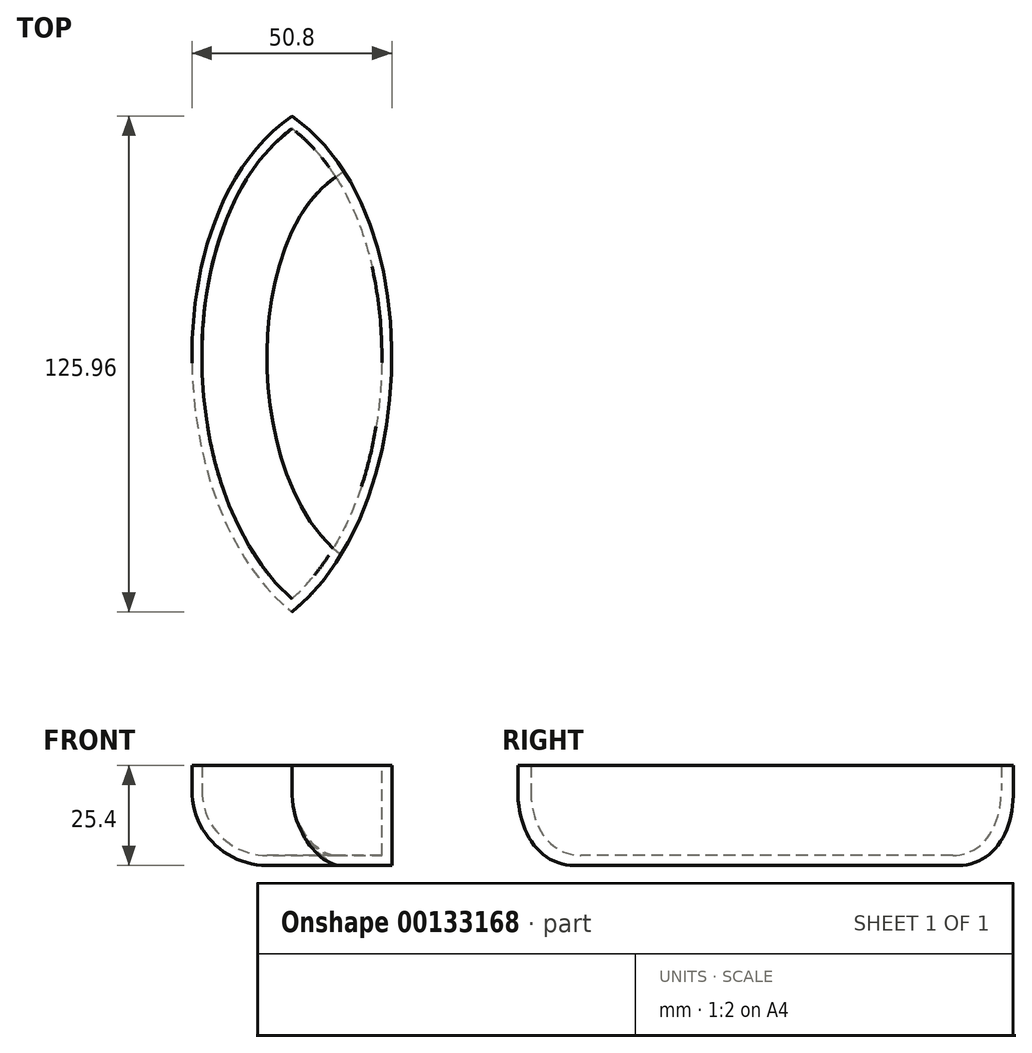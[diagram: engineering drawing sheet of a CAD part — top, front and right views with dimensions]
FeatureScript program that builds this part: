
annotation { "Feature Type Name" : "Feature", "Feature Type Description" : "" }
export const myFeature = defineFeature(function(context is Context, id is Id, definition is map)
    precondition{}
    {
        {
            var Q0;
            Q0=qCreatedBy(makeId("Top.planeOp"),FACE);
            var sketch = newSketch(context, id + "F0", { "sketchPlane" : qUnion([Q0])});
            skFitSpline(sketch, "E0", {"points": [v(0, 61.2) * mm, v(0, -64.75) * mm], "startDerivative": vector(-104.4, -72) * mm, "endDerivative": vector(98.77, -79.04) * mm});
            skFitSpline(sketch, "E1.MirrorCS", {"points": [v(0, 61.2) * mm, v(0, -64.75) * mm], "startDerivative": vector(104.4, -72) * mm, "endDerivative": vector(-98.77, -79.04) * mm});
            skFitSpline(sketch, "E2.MirrorCS", {"points": [v(0, 61.2) * mm, v(0, -64.75) * mm], "startDerivative": vector(104.4, -72) * mm, "endDerivative": vector(-98.77, -79.04) * mm});
            skLineSegment(sketch, "E3", {"start": v(-25.4, 0) * mm, "end": v(25.4, 0) * mm, "construction": true});
            skSolve(sketch);
        }
        {
            var Q0;
            Q0=makeQuery(id+"F0.imprint","IMPRINT",FACE,{"disambiguationData":[TD([[makeQuery(id+"F0.imprint","IMPRINT",EDGE,{"derivedFrom":sQuery(id+"F0.wireOp",EDGE,"E0")}),1.0]])]});
            extrude(context, id + "F1", {"entities" : qUnion([Q0]), "depth" : 25.4 * mm});
        }
        {
            var Q0;
            Q0=makeQuery(id+"F1.opExtrude","CAP_EDGE",EDGE,{"disambiguationData":[OSD([sQuery(id+"F0.wireOp",EDGE,"E2.MirrorCS")])],"isStart":true});
            var Q1;
            Q1=makeQuery(id+"F1.opExtrude","CAP_EDGE",EDGE,{"disambiguationData":[OSD([sQuery(id+"F0.wireOp",EDGE,"E0")])],"isStart":true});
            fillet(context, id + "F2", {"entities" : qUnion([Q0, Q1]), "radius" : 19.05 * mm, "tangentPropagation" : true, "allowEdgeOverflow" : false});
        }
        {
            var Q0;
            Q0=makeQuery(id+"F1.opExtrude","CAP_FACE",FACE,{"disambiguationData":[OSD([sQuery(id+"F0.wireOp",EDGE,"E0"),sQuery(id+"F0.wireOp",EDGE,"E2.MirrorCS")])],"isStart":false});
            shell(context, id + "F3", {"entities" : qUnion([Q0]), "thickness" : 2.54 * mm});
        }
    });
